# Revit family: Турникет трипод PERCo_TTR-04, 07
name_source: partatom
category: Mechanical Equipment
units: mm (PartAtom-declared; Revit-internal decimal feet)

## family parameters
Always vertical = Yes
Classification = None
Cut with Voids When Loaded = No
Part Type = Normal
Room Calculation Point = No
Round Connector Dimension = Use Diameter
Shared = No
Work Plane-Based = No

## types (3) — shared parameters
Built-in reader = not provided
Electrical connection = 220 V
Manufacturer = PERCo
Material = Housing ─ powder-coated steel. Barrier arms ─ stainless steel.
Maximum dimensions of ACS controller = not provided
Maximum dimensions of installed readers = not provided
Number = 1
Plank length = 554 mm  [stored 1.81759 ft]
Throughput rate = 30 persons/min
URL = https://www.perco.com
Unit of measurement = pcs
Voltage = 12 V

## per-type parameters (varying)
| type | Colour | Current | Dimensions | Full name | IP Code | Name | Operating temperature | Passageway width | Rated power | Turnstile coloring | Weight |
| Turnstile TTR-04CW | light beige colour with pearl mica effect | 1 A | 855×810×1050 | TTR-04CW Electromechanical Tripod Turnstile for outdoor application | IP42 | TTR-04CW Tripod Turnstile | from -40°С to +50°С | 600 mm | 9 W | Light beige with mica effect | max. 37 kg |
| Turnstile TTR-04.1 | light beige colour with pearl mica effect; dark grey colour with pearl mica effect; glitter black colour with lacquered finish | 1 A | 855×810×1050 | TTR-04.1 Electromechanical Tripod Turnstile for indoor application | IP41 | TTR-04.1 Tripod Turnstile | from +1°С to +50°С | 600 mm | 9 W | Dark gray with mica effect | max. 30 kg |
| Turnstile TTR-07.1 | dark grey colour with pearl mica effect | 6 A | 798×752×1054 | TTR-07.1 Electromechanical Tripod Turnstile with Automatic Anti-Panic Barrier Arms
TTR-07.1 Electromechanical Tripod Turnstile with Automatic Anti-Panic Barrier Arms
TTR-07.1 Electromechanical Tripod Turnstile with Automatic Anti-Panic Barrier Arms | IP41 | TTR-07.1 Tripod Turnstile | from +1°С to +50°С | 530 mm | 72 W | Dark gray with mica effect | max. 36 kg |

note: [stored X ft] marks values corroborated as IEEE doubles in the binary element streams (Revit-internal decimal feet)
